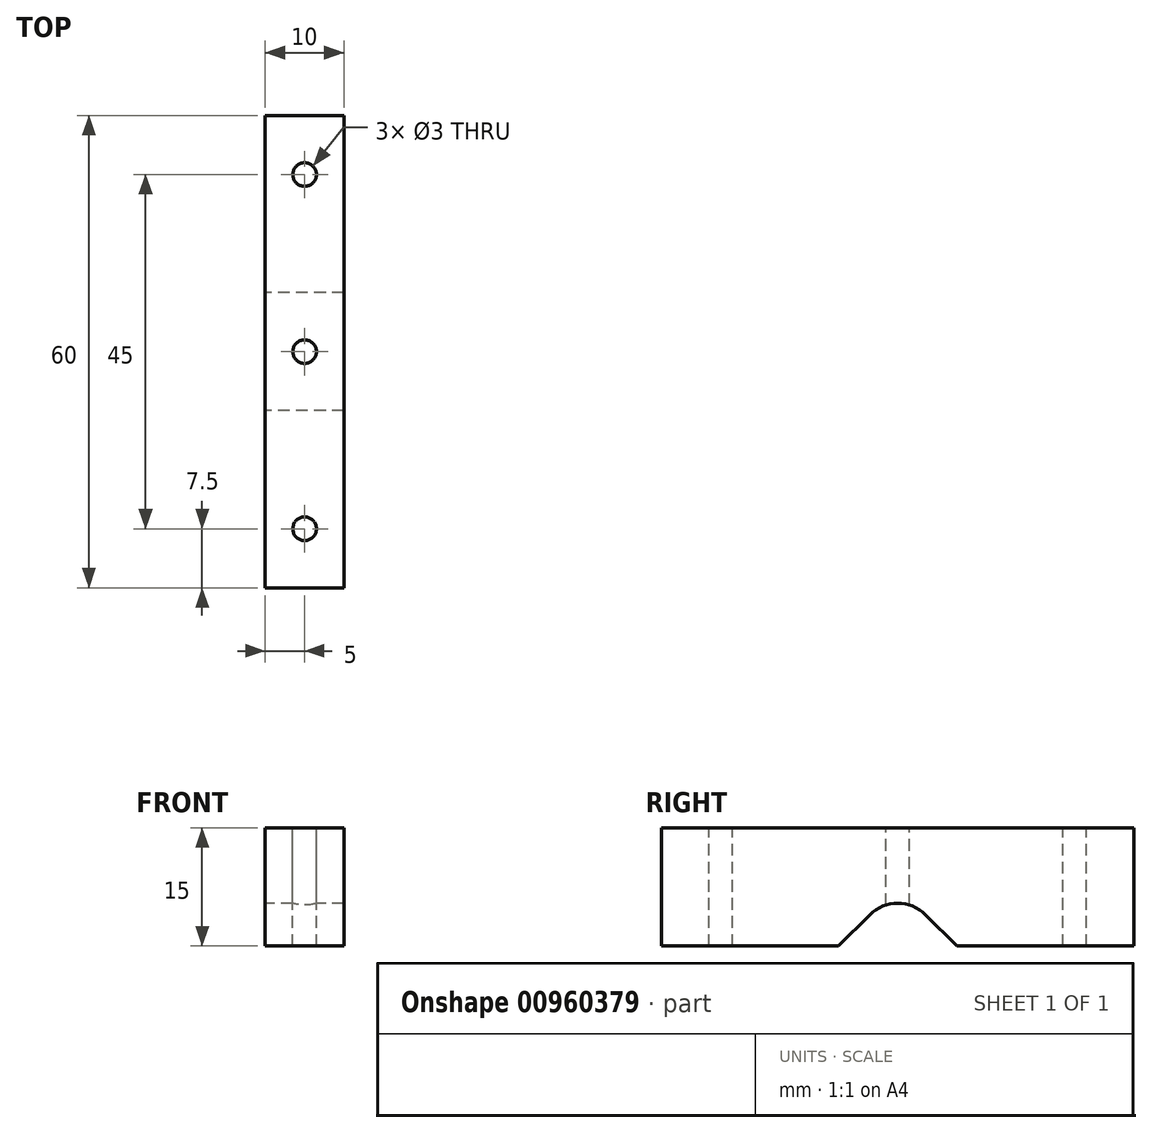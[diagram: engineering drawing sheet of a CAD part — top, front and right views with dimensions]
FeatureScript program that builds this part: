
annotation { "Feature Type Name" : "Feature", "Feature Type Description" : "" }
export const myFeature = defineFeature(function(context is Context, id is Id, definition is map)
    precondition{}
    {
        {
            var Q0;
            Q0=qCreatedBy(makeId("Right.planeOp"),FACE);
            var sketch = newSketch(context, id + "F0", { "sketchPlane" : qUnion([Q0])});
            skLineSegment(sketch, "E0.top", {"start": v(-30, 15) * mm, "end": v(30, 15) * mm});
            skLineSegment(sketch, "E0.left", {"start": v(-30, 0) * mm, "end": v(-30, 15) * mm});
            skLineSegment(sketch, "E0.right", {"start": v(30, 0) * mm, "end": v(30, 15) * mm});
            skLineSegment(sketch, "E1", {"start": v(-30, 0) * mm, "end": v(-7.5, 0) * mm});
            skLineSegment(sketch, "E2", {"start": v(-7.5, 0) * mm, "end": v(-3.54, 3.96) * mm});
            skLineSegment(sketch, "E3", {"start": v(3.54, 3.96) * mm, "end": v(7.5, 0) * mm});
            skLineSegment(sketch, "E4", {"start": v(7.5, 0) * mm, "end": v(30, 0) * mm});
            skPoint(sketch, "E5.visualSharp", {"position": v(0, 7.5) * mm});
            skArc(sketch, "E5.filletArc", {"start": v(3.54, 3.96) * mm, "mid": v(0, 5.43) * mm, "end": v(-3.54, 3.96) * mm});
            skSolve(sketch);
        }
        {
            var Q0;
            Q0 = qSketchRegion(id + "F0", true);
            extrude(context, id + "F1", {"entities" : qUnion([Q0]), "depth" : 10 * mm, "offsetDistance" : 25 * mm});
        }
        {
            var Q0;
            Q0=makeQuery(id+"F1.opExtrude","SWEPT_FACE",FACE,{"disambiguationData":[OSD([sQuery(id+"F0.wireOp",EDGE,"E0.top")])]});
            var sketch = newSketch(context, id + "F2", { "sketchPlane" : qUnion([Q0])});
            skCircle(sketch, "E6", {"center": v(5, 0) * mm, "radius": 1.5 * mm});
            skCircle(sketch, "E7", {"center": v(5, 22.5) * mm, "radius": 1.5 * mm});
            skPoint(sketch, "E7.centerSnap0", {"position": v(5, 30) * mm});
            skCircle(sketch, "E8", {"center": v(5, -22.5) * mm, "radius": 1.5 * mm});
            skPoint(sketch, "E8.centerSnap0", {"position": v(5, -30) * mm});
            skSolve(sketch);
        }
        {
            var Q0;
            Q0 = qSketchRegion(id + "F2", true);
            extrude(context, id + "F3", {"entities" : qUnion([Q0]), "operationType" : NewBodyOperationType.REMOVE, "endBound" : BoundingType.UP_TO_NEXT, "oppositeDirection" : true, "depth" : 25 * mm, "offsetDistance" : 25 * mm});
        }
    });
